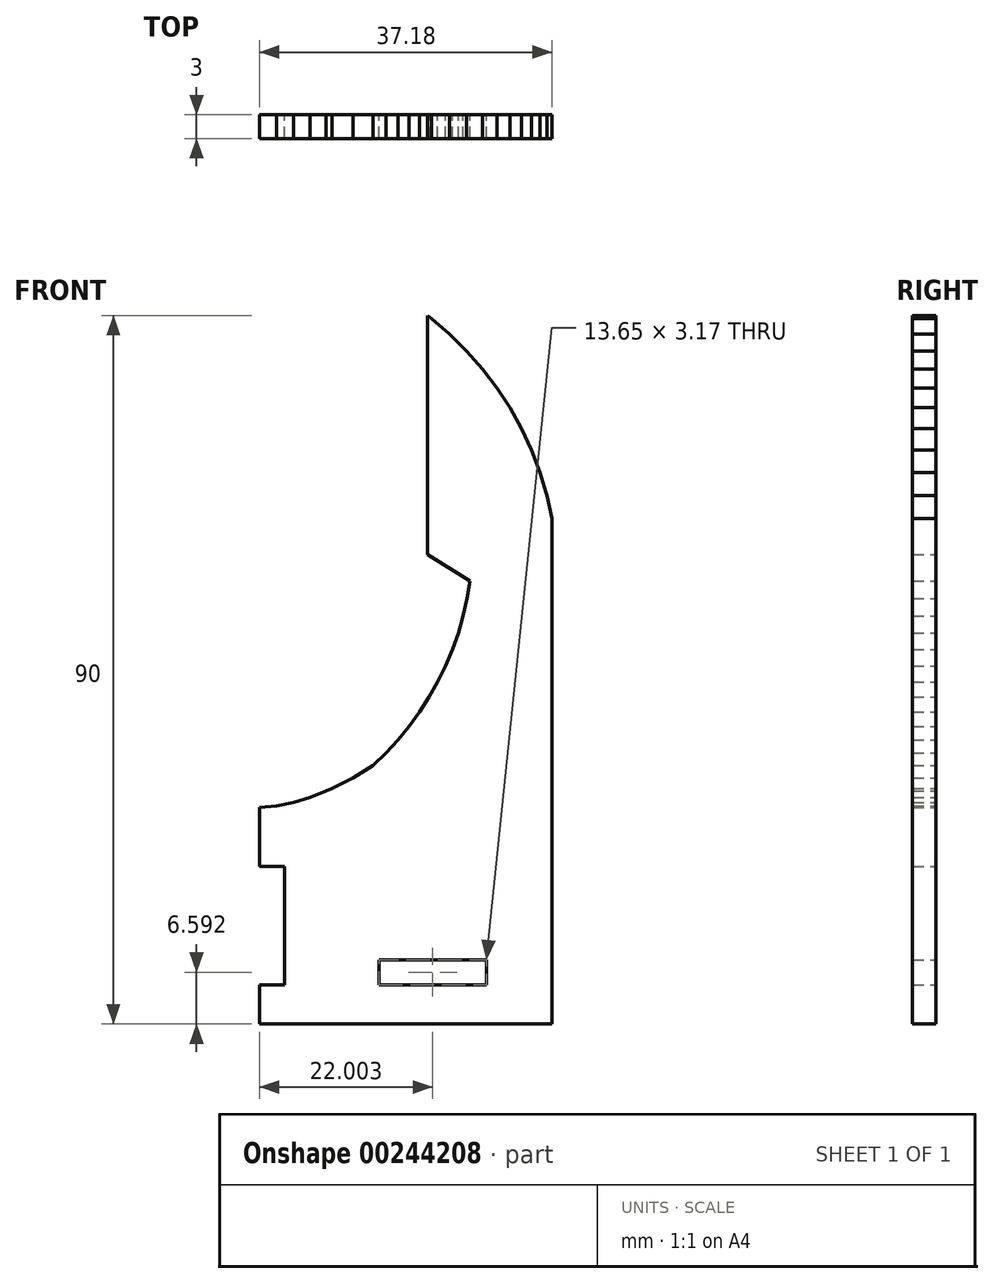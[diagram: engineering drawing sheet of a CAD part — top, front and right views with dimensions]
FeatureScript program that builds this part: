
annotation { "Feature Type Name" : "Feature", "Feature Type Description" : "" }
export const myFeature = defineFeature(function(context is Context, id is Id, definition is map)
    precondition{}
    {
        {
            var Q0;
            Q0=qCreatedBy(makeId("Front.planeOp"),FACE);
            var sketch = newSketch(context, id + "F0", { "sketchPlane" : qUnion([Q0])});
            skLineSegment(sketch, "E0", {"start": v(2.75, 14.63) * mm, "end": v(8.16, 11.26) * mm});
            skLineSegment(sketch, "E1", {"start": v(8.16, 11.26) * mm, "end": v(7.79, 9.04) * mm});
            skLineSegment(sketch, "E2", {"start": v(7.79, 9.04) * mm, "end": v(7.29, 6.85) * mm});
            skLineSegment(sketch, "E3", {"start": v(7.29, 6.85) * mm, "end": v(6.66, 4.7) * mm});
            skLineSegment(sketch, "E4", {"start": v(6.66, 4.7) * mm, "end": v(5.91, 2.58) * mm});
            skLineSegment(sketch, "E5", {"start": v(5.91, 2.58) * mm, "end": v(5.04, 0.5) * mm});
            skLineSegment(sketch, "E6", {"start": v(5.04, 0.5) * mm, "end": v(4.05, -1.51) * mm});
            skLineSegment(sketch, "E7", {"start": v(4.05, -1.51) * mm, "end": v(2.95, -3.47) * mm});
            skLineSegment(sketch, "E8", {"start": v(2.95, -3.47) * mm, "end": v(1.74, -5.36) * mm});
            skLineSegment(sketch, "E9", {"start": v(1.74, -5.36) * mm, "end": v(0.42, -7.18) * mm});
            skLineSegment(sketch, "E10", {"start": v(0.42, -7.18) * mm, "end": v(-1, -8.91) * mm});
            skLineSegment(sketch, "E11", {"start": v(-1, -8.91) * mm, "end": v(-2.52, -10.57) * mm});
            skLineSegment(sketch, "E12", {"start": v(-2.52, -10.57) * mm, "end": v(-4.14, -12.13) * mm});
            skLineSegment(sketch, "E13", {"start": v(-4.14, -12.13) * mm, "end": v(-6.68, -13.73) * mm});
            skLineSegment(sketch, "E14", {"start": v(-6.68, -13.73) * mm, "end": v(-9.36, -15.1) * mm});
            skLineSegment(sketch, "E15", {"start": v(-9.36, -15.1) * mm, "end": v(-10.11, -15.39) * mm});
            skLineSegment(sketch, "E16", {"start": v(-10.11, -15.39) * mm, "end": v(-12.14, -16.22) * mm});
            skLineSegment(sketch, "E17", {"start": v(-12.14, -16.22) * mm, "end": v(-14.25, -16.85) * mm});
            skLineSegment(sketch, "E18", {"start": v(-14.25, -16.85) * mm, "end": v(-16.4, -17.26) * mm});
            skLineSegment(sketch, "E19", {"start": v(-16.4, -17.26) * mm, "end": v(-18.59, -17.46) * mm});
            skLineSegment(sketch, "E20", {"start": v(-18.59, -17.46) * mm, "end": v(-18.59, -25) * mm});
            skLineSegment(sketch, "E21", {"start": v(-18.59, -25) * mm, "end": v(-15.41, -25) * mm});
            skLineSegment(sketch, "E22", {"start": v(-15.41, -25) * mm, "end": v(-15.41, -40) * mm});
            skLineSegment(sketch, "E23", {"start": v(-15.41, -40) * mm, "end": v(-18.59, -40) * mm});
            skLineSegment(sketch, "E24", {"start": v(-18.59, -40) * mm, "end": v(-18.59, -45) * mm});
            skLineSegment(sketch, "E25", {"start": v(-18.59, -45) * mm, "end": v(18.59, -45) * mm});
            skLineSegment(sketch, "E26", {"start": v(18.59, -45) * mm, "end": v(18.59, 19.22) * mm});
            skLineSegment(sketch, "E27", {"start": v(18.59, 19.22) * mm, "end": v(17.92, 22.17) * mm});
            skLineSegment(sketch, "E28", {"start": v(17.92, 22.17) * mm, "end": v(17.82, 22.5) * mm});
            skLineSegment(sketch, "E29", {"start": v(17.82, 22.5) * mm, "end": v(17.04, 25.07) * mm});
            skLineSegment(sketch, "E30", {"start": v(17.04, 25.07) * mm, "end": v(15.96, 27.9) * mm});
            skLineSegment(sketch, "E31", {"start": v(15.96, 27.9) * mm, "end": v(14.68, 30.64) * mm});
            skLineSegment(sketch, "E32", {"start": v(14.68, 30.64) * mm, "end": v(13.2, 33.29) * mm});
            skLineSegment(sketch, "E33", {"start": v(13.2, 33.29) * mm, "end": v(11.55, 35.83) * mm});
            skLineSegment(sketch, "E34", {"start": v(11.55, 35.83) * mm, "end": v(9.72, 38.24) * mm});
            skLineSegment(sketch, "E35", {"start": v(9.72, 38.24) * mm, "end": v(7.73, 40.51) * mm});
            skLineSegment(sketch, "E36", {"start": v(7.73, 40.51) * mm, "end": v(5.57, 42.64) * mm});
            skLineSegment(sketch, "E37", {"start": v(5.57, 42.64) * mm, "end": v(3.27, 44.61) * mm});
            skLineSegment(sketch, "E38", {"start": v(3.27, 44.61) * mm, "end": v(2.75, 45) * mm});
            skLineSegment(sketch, "E39", {"start": v(2.75, 45) * mm, "end": v(2.75, 44.61) * mm});
            skLineSegment(sketch, "E40", {"start": v(2.75, 44.61) * mm, "end": v(2.75, 14.63) * mm});
            skLineSegment(sketch, "E41", {"start": v(10.24, -36.82) * mm, "end": v(10.24, -40) * mm});
            skLineSegment(sketch, "E42", {"start": v(10.24, -40) * mm, "end": v(-3.41, -40) * mm});
            skLineSegment(sketch, "E43", {"start": v(-3.41, -40) * mm, "end": v(-3.41, -36.82) * mm});
            skLineSegment(sketch, "E44", {"start": v(-3.41, -36.82) * mm, "end": v(10.24, -36.82) * mm});
            skSolve(sketch);
        }
        {
            var Q0;
            Q0 = qSketchRegion(id + "F0", true);
            extrude(context, id + "F1", {"entities" : qUnion([Q0]), "depth" : 3 * mm});
        }
    });
